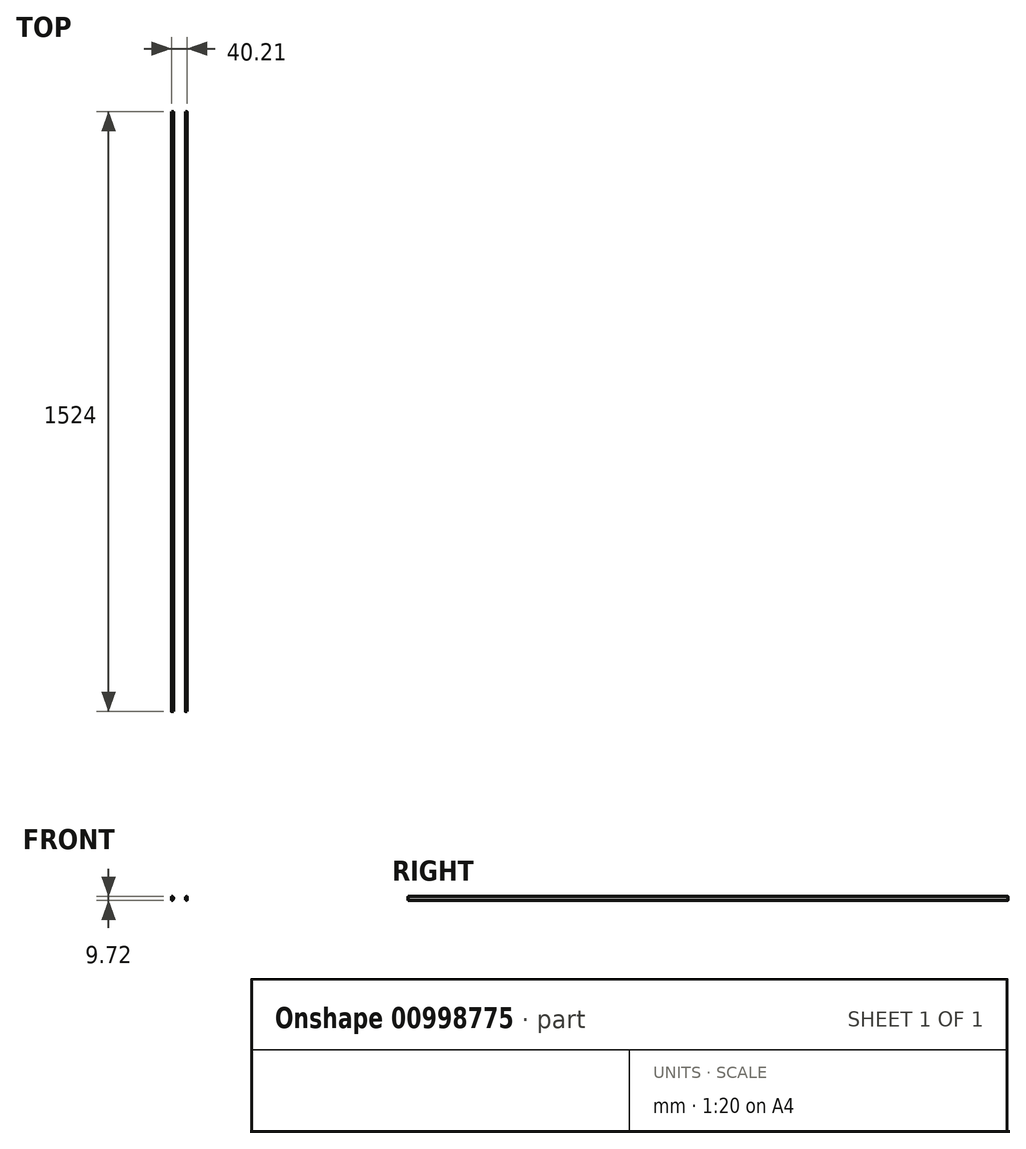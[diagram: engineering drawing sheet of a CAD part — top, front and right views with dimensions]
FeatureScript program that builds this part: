
annotation { "Feature Type Name" : "Feature", "Feature Type Description" : "" }
export const myFeature = defineFeature(function(context is Context, id is Id, definition is map)
    precondition{}
    {
        {
            var Q0;
            Q0=qCreatedBy(makeId("Front.planeOp"),FACE);
            var sketch = newSketch(context, id + "F0", { "sketchPlane" : qUnion([Q0])});
            skCircle(sketch, "E0", {"center": v(-48.95, 0) * mm, "radius": 5.08 * mm});
            skLineSegment(sketch, "E1", {"start": v(-48.95, 0) * mm, "end": v(-43.87, 0) * mm});
            skLineSegment(sketch, "E2", {"start": v(-43.87, 0) * mm, "end": v(-13.82, 0) * mm});
            skLineSegment(sketch, "E3", {"start": v(-13.82, 0) * mm, "end": v(-8.74, 0) * mm});
            skCircle(sketch, "E4", {"center": v(-8.74, 0) * mm, "radius": 5.08 * mm});
            skLineSegment(sketch, "E5", {"start": v(-48.95, 0) * mm, "end": v(-48.95, 5.08) * mm});
            skLineSegment(sketch, "E6", {"start": v(-48.95, 5.08) * mm, "end": v(-48.95, -8.9) * mm});
            skLineSegment(sketch, "E7", {"start": v(-8.74, 0) * mm, "end": v(-8.74, 5.08) * mm});
            skLineSegment(sketch, "E8", {"start": v(-8.74, 5.08) * mm, "end": v(-8.74, -8.9) * mm});
            skLineSegment(sketch, "E9", {"start": v(-8.74, -8.9) * mm, "end": v(-48.95, -8.9) * mm});
            skLineSegment(sketch, "E10.bottom", {"start": v(-48.95, -8.9) * mm, "end": v(-8.74, -8.9) * mm});
            skLineSegment(sketch, "E10.top", {"start": v(-48.95, -3.56) * mm, "end": v(-8.74, -3.56) * mm});
            skLineSegment(sketch, "E10.left", {"start": v(-48.95, -8.9) * mm, "end": v(-48.95, -3.56) * mm});
            skLineSegment(sketch, "E10.right", {"start": v(-8.74, -8.9) * mm, "end": v(-8.74, -3.56) * mm});
            skSolve(sketch);
        }
        {
            var Q0;
            {var subQ0=sQuery(id+"F0.wireOp",EDGE,"E1");Q0=makeQuery(id+"F0.imprint","IMPRINT",FACE,{"disambiguationData":[TD([[makeQuery(id+"F0.imprint","IMPRINT",EDGE,{"derivedFrom":subQ0}),-1.0]])]});}
            var Q1;
            {var subQ0=sQuery(id+"F0.wireOp",EDGE,"E1");Q1=makeQuery(id+"F0.imprint","IMPRINT",FACE,{"disambiguationData":[TD([[makeQuery(id+"F0.imprint","IMPRINT",EDGE,{"derivedFrom":subQ0}),1.0]])]});}
            var Q2;
            {var subQ0=sQuery(id+"F0.wireOp",EDGE,"E10.left");var subQ1=sQuery(id+"F0.wireOp",EDGE,"E0");var subQ2=makeQuery(id+"F0.imprint","INTERSECT",VERTEX,{"derivedFrom":[subQ1,subQ0]});Q2=makeQuery(id+"F0.imprint","IMPRINT",FACE,{"disambiguationData":[TD([[makeQuery(id+"F0.imprint","IMPRINT",EDGE,{"disambiguationData":[TD([[subQ2,-1.0]])],"derivedFrom":subQ1}),1.0]])]});}
            var Q3;
            {var subQ0=sQuery(id+"F0.wireOp",EDGE,"E6");var subQ1=sQuery(id+"F0.wireOp",EDGE,"E0");var subQ2=makeQuery(id+"F0.imprint","INTERSECT",VERTEX,{"derivedFrom":[subQ1,subQ0]});Q3=makeQuery(id+"F0.imprint","IMPRINT",FACE,{"disambiguationData":[TD([[makeQuery(id+"F0.imprint","IMPRINT",EDGE,{"disambiguationData":[TD([[subQ2,-1.0]])],"derivedFrom":subQ1}),1.0]])]});}
            var Q4;
            {var subQ0=sQuery(id+"F0.wireOp",EDGE,"E10.bottom");Q4=makeQuery(id+"F0.imprint","IMPRINT",FACE,{"disambiguationData":[TD([[makeQuery(id+"F0.imprint","IMPRINT",EDGE,{"derivedFrom":subQ0}),1.0]])]});}
            var Q5;
            {var subQ0=sQuery(id+"F0.wireOp",EDGE,"E3");Q5=makeQuery(id+"F0.imprint","IMPRINT",FACE,{"disambiguationData":[TD([[makeQuery(id+"F0.imprint","IMPRINT",EDGE,{"derivedFrom":subQ0}),-1.0]])]});}
            var Q6;
            {var subQ0=sQuery(id+"F0.wireOp",EDGE,"E3");Q6=makeQuery(id+"F0.imprint","IMPRINT",FACE,{"disambiguationData":[TD([[makeQuery(id+"F0.imprint","IMPRINT",EDGE,{"derivedFrom":subQ0}),1.0]])]});}
            var Q7;
            {var subQ0=sQuery(id+"F0.wireOp",EDGE,"E10.right");var subQ1=sQuery(id+"F0.wireOp",EDGE,"E4");var subQ2=makeQuery(id+"F0.imprint","INTERSECT",VERTEX,{"derivedFrom":[subQ1,subQ0]});Q7=makeQuery(id+"F0.imprint","IMPRINT",FACE,{"disambiguationData":[TD([[makeQuery(id+"F0.imprint","IMPRINT",EDGE,{"disambiguationData":[TD([[subQ2,1.0]])],"derivedFrom":subQ1}),1.0]])]});}
            var Q8;
            {var subQ0=sQuery(id+"F0.wireOp",EDGE,"E8");var subQ1=sQuery(id+"F0.wireOp",EDGE,"E4");var subQ2=makeQuery(id+"F0.imprint","INTERSECT",VERTEX,{"derivedFrom":[subQ1,subQ0]});Q8=makeQuery(id+"F0.imprint","IMPRINT",FACE,{"disambiguationData":[TD([[makeQuery(id+"F0.imprint","IMPRINT",EDGE,{"disambiguationData":[TD([[subQ2,1.0]])],"derivedFrom":subQ1}),1.0]])]});}
            extrude(context, id + "F1", {"entities" : qUnion([Q0, Q1, Q2, Q3, Q4, Q5, Q6, Q7, Q8]), "depth" : 1524 * mm, "offsetDistance" : 25.4 * mm});
        }
        {
            var Q0;
            Q0=makeQuery(id+"F1.opExtrude","SWEPT_EDGE",EDGE,{"disambiguationData":[OSD([sQuery(id+"F0.wireOp",EDGE,"E0"),sQuery(id+"F0.wireOp",EDGE,"E10.top")])]});
            var Q1;
            Q1=makeQuery(id+"F1.opExtrude","SWEPT_EDGE",EDGE,{"disambiguationData":[OSD([sQuery(id+"F0.wireOp",EDGE,"E4"),sQuery(id+"F0.wireOp",EDGE,"E10.top")])]});
            fillet(context, id + "F2", {"entities" : qUnion([Q0, Q1]), "radius" : 1.27 * mm, "tangentPropagation" : true, "allowEdgeOverflow" : false});
        }
    });
